# Revit family: Faucet-Handle-KOHLER-COMPOSED-K-20449T
name_source: partatom
category: Specialty Equipment
revit_build: Autodesk Revit 2017 (Build: 20160225_1515(x64)
units: mm (PartAtom-declared; Revit-internal decimal feet)

## family parameters
Cut with Voids When Loaded = No
Host = Face
OmniClass Number = 23.31.25.00
Part Type = Normal
Room Calculation Point = No
Round Connector Dimension = Use Diameter
Shared = No

## types (4) — shared parameters
ADA Compliant = No
Assembly Code = C1030200
Date Modified = 10/18/2021
Default Elevation = 42"
Description = Composed Faucet Lavatory Handles
Height = 1 5/16"
Length = 1 7/16"
Manufacturer = KOHLER Co.
Master Format 2014 = 10 28 00
Master Format 2014 Name = Toilet, Bath, and Laundry Accessories
Material = Brass Construction
Product Name = COMPOSED
URL = http://www.kohler.com.cn
WaterSense Certified = No
Width = 1 5/16"

## per-type parameters (varying)
| type | Finish | Model | Type |
| 0-White | Kohler-Metal-0-White | K-20449T-B7-0 | 1 |
| BL-Matte Black | Kohler-Metal-BL-Matte_Black | K-20449T-B7-BL | 2 |
| RGD-Rose Gold | Kohler-Metal-RGD-Rose_Gold | K-20449T-B7-RGD | 3 |
| TT-Titanium Silver | Kohler-Metal-TT-Titanium_Silver | K-20449T-B7-TT | 4 |

## geometry (parser evidence)
native form markers: Sweep x6
no freeform markers — native parametric forms only
